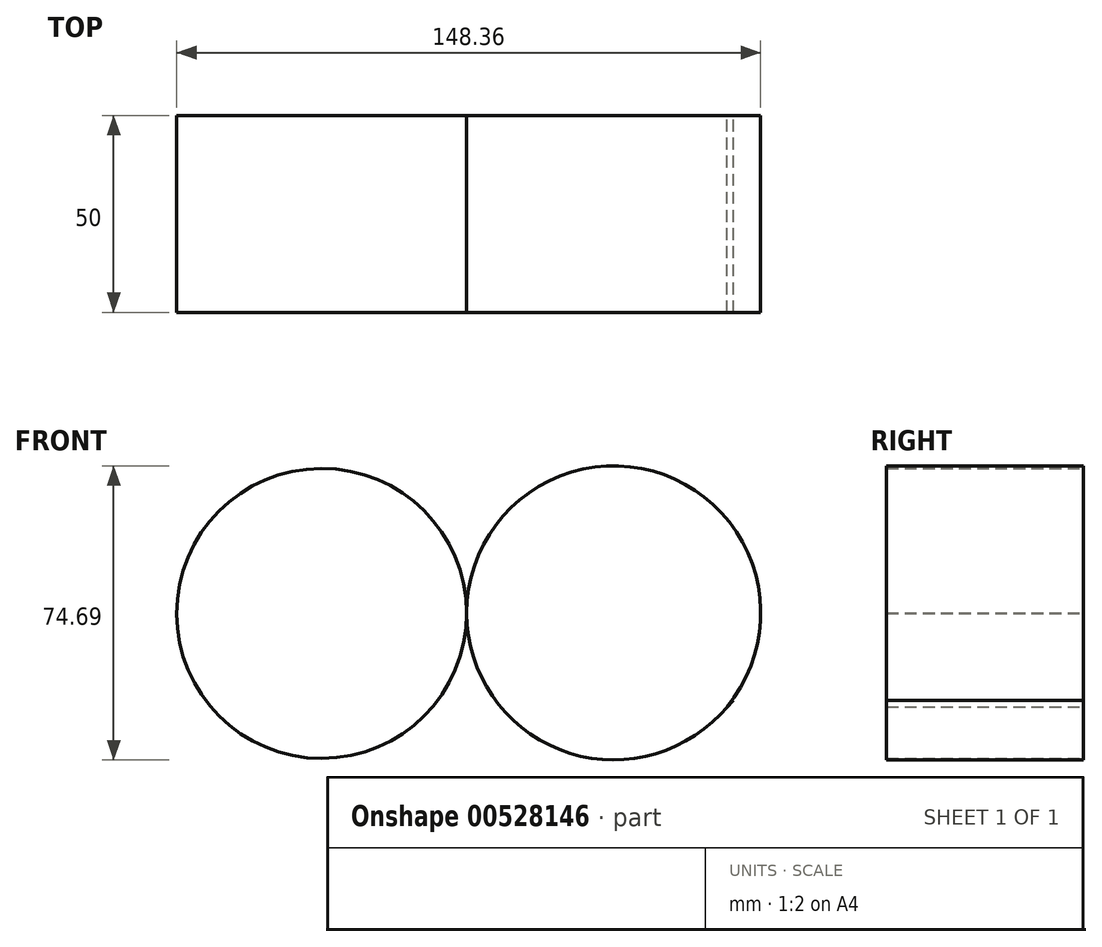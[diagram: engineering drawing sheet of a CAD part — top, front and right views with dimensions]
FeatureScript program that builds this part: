
annotation { "Feature Type Name" : "Feature", "Feature Type Description" : "" }
export const myFeature = defineFeature(function(context is Context, id is Id, definition is map)
    precondition{}
    {
        {
            var Q0;
            Q0=qCreatedBy(makeId("Front.planeOp"),FACE);
            var sketch = newSketch(context, id + "F0", { "sketchPlane" : qUnion([Q0])});
            skCircle(sketch, "E0", {"center": v(-36.83, 37.69) * mm, "radius": 36.83 * mm});
            skPoint(sketch, "E0.first.point", {"position": v(0, 37.87) * mm});
            skPoint(sketch, "E0.second.point", {"position": v(-73.64, 36.3) * mm});
            skPoint(sketch, "E0.third.point", {"position": v(-66.3, 15.6) * mm});
            skCircle(sketch, "E1", {"center": v(37.34, 37.82) * mm, "radius": 37.34 * mm});
            skPoint(sketch, "E1.second.point", {"position": v(74.69, 37.87) * mm});
            skPoint(sketch, "E1.third.point", {"position": v(52.15, 3.54) * mm});
            skLineSegment(sketch, "E2", {"start": v(-64.4, 13.26) * mm, "end": v(0, -55.69) * mm});
            skLineSegment(sketch, "E3", {"start": v(0, -55.69) * mm, "end": v(67.74, 15.6) * mm});
            skLineSegment(sketch, "E4", {"start": v(67.74, 15.6) * mm, "end": v(66.05, 13.94) * mm});
            skSolve(sketch);
        }
        {
            var Q0;
            {var subQ0=sQuery(id+"F0.wireOp",EDGE,"E2");var subQ1=sQuery(id+"F0.wireOp",EDGE,"E0");var subQ2=makeQuery(id+"F0.imprint","INTERSECT",VERTEX,{"disambiguationData":[OD(0.0)],"derivedFrom":[subQ1,subQ0]});Q0=makeQuery(id+"F0.imprint","IMPRINT",FACE,{"disambiguationData":[TD([[makeQuery(id+"F0.imprint","IMPRINT",EDGE,{"disambiguationData":[TD([[subQ2,-1.0]])],"derivedFrom":subQ1}),1.0]])]});}
            var Q1;
            {var subQ0=sQuery(id+"F0.wireOp",EDGE,"E4");Q1=makeQuery(id+"F0.imprint","IMPRINT",FACE,{"disambiguationData":[TD([[makeQuery(id+"F0.imprint","IMPRINT",EDGE,{"derivedFrom":subQ0}),1.0]])]});}
            var Q2;
            {var subQ0=sQuery(id+"F0.wireOp",EDGE,"E1");var subQ1=sQuery(id+"F0.wireOp",EDGE,"E0");var subQ2=makeQuery(id+"F0.imprint","INTERSECT",VERTEX,{"disambiguationData":[OD(0.0)],"derivedFrom":[subQ1,subQ0]});Q2=makeQuery(id+"F0.imprint","IMPRINT",FACE,{"disambiguationData":[TD([[makeQuery(id+"F0.imprint","IMPRINT",EDGE,{"disambiguationData":[TD([[subQ2,1.0]])],"derivedFrom":subQ1}),1.0]])]});}
            var Q3;
            {var subQ0=sQuery(id+"F0.wireOp",EDGE,"E2");var subQ1=sQuery(id+"F0.wireOp",EDGE,"E0");var subQ2=makeQuery(id+"F0.imprint","INTERSECT",VERTEX,{"disambiguationData":[OD(0.0)],"derivedFrom":[subQ1,subQ0]});Q3=makeQuery(id+"F0.imprint","IMPRINT",FACE,{"disambiguationData":[TD([[makeQuery(id+"F0.imprint","IMPRINT",EDGE,{"disambiguationData":[TD([[subQ2,1.0]])],"derivedFrom":subQ1}),1.0]])]});}
            var Q4;
            {var subQ0=sQuery(id+"F0.wireOp",EDGE,"E1");var subQ1=sQuery(id+"F0.wireOp",EDGE,"E0");var subQ2=makeQuery(id+"F0.imprint","INTERSECT",VERTEX,{"disambiguationData":[OD(0.0)],"derivedFrom":[subQ1,subQ0]});Q4=makeQuery(id+"F0.imprint","IMPRINT",FACE,{"disambiguationData":[TD([[makeQuery(id+"F0.imprint","IMPRINT",EDGE,{"disambiguationData":[TD([[subQ2,1.0]])],"derivedFrom":subQ1}),-1.0]])]});}
            var Q5;
            {var subQ0=sQuery(id+"F0.wireOp",EDGE,"E2");var subQ1=sQuery(id+"F0.wireOp",EDGE,"E0");var subQ2=makeQuery(id+"F0.imprint","INTERSECT",VERTEX,{"disambiguationData":[OD(1.0)],"derivedFrom":[subQ1,subQ0]});Q5=makeQuery(id+"F0.imprint","IMPRINT",FACE,{"disambiguationData":[TD([[makeQuery(id+"F0.imprint","IMPRINT",EDGE,{"disambiguationData":[TD([[subQ2,-1.0]])],"derivedFrom":subQ1}),-1.0]])]});}
            extrude(context, id + "F1", {"entities" : qUnion([Q0, Q1, Q2, Q3, Q4, Q5]), "depth" : 50 * mm, "offsetDistance" : 25 * mm});
        }
    });
